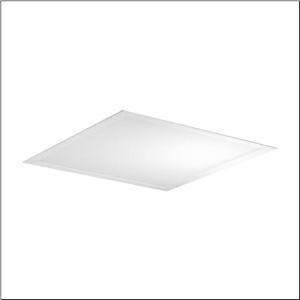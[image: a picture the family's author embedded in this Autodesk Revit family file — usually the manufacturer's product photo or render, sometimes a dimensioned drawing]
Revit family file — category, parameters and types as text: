
# Revit family: apollon_r__31_square_51mp11w72342_58c9
name_source: partatom
category: Lighting Fixtures
units: mm (PartAtom-declared; Revit-internal decimal feet)

## family parameters
Cut with Voids When Loaded = No
Host = Face
Light Source = No
Part Type = Normal
Room Calculation Point = No
Round Connector Dimension = Use Diameter
Shared = No

## types (1)
- Apollon® 31 square (1 x LED, 3800 lm, 27.5 W, 3000K)
    Apparent Load = 28 VA
    CIE Flux Codes = 61 87 97 100 100
    Color Rendering = 80
    Color Temperature = 3000K
    Default Elevation = 1800 mm
    Description = Apollon® 31 square, office luminaire, primary optical cover: micro prismatic cover, of PMMA, CAT 2 (L<= 3000cd/m²), light emission: direct distribution, primary light characteristic: symmetric, installation type: lay-in mounting, LED, rated luminous flux: 3.800lm, luminous efficacy: 138lm/W, light colour: 830, colour temperature: 3000K, with terminal, 3-pole, mains connection: 220..240V, AC, 50/60Hz, rated input power: 28W, housing, of aluminium, traffic white (RAL 9016), module: M625, length: 620mm, width: 620mm, height: 32mm, housing upper side, of sheet steel, galvanised, protection rating (complete): IP20, protection rating (on room side): IP40, insulation class (complete): insulation class II (safety insulation), certification: CE, ENEC, impact resistance: IK03, permissible operating ambient temperature: -20..+40°C, permissible storage temperature: -20..+60°C, packaging unit: 1 piece
    Height = 0 mm  [stored 0 ft]
    Lamp = 1 x LED
    Lamp Light Flux = 3800 lm
    Lamp Power = 27.5 W
    Lamp count = 1
    Length = 620 mm
    Luminous efficacy = 138 lm/W
    Manufacturer = Siteco
    ModVariant = No
    Model = 51MP11W72342
    Mounting Place = Ceiling
    Mounting Type = Recessed
    Number of Poles = 1
    OnlyDefault = Yes
    Power Factor = 1
    Product Name = Apollon® 31 square
    Product group = office luminaire | ceiling recessed
    ProductGroupID = 401
    Protection Class = Protection class II
    Protection Degree = IP 20
    RLX_Detail_Level = 1
    RLX_Emergency_Light_Flux = 0 lm
    RLX_Emergency_Type = 0
    RLX_Emergency_Type_DB = No
    RlxData = <blob elided: 12933 chars, md5=674a0db6>
    Socket = socket
    Standby Power = 0 W
    System Light Flux = 3800 lm
    System Power = 28 W
    Type Comments = Product without accessories
    Type Image = l_1291039.jpg
    URL = http://relux.com
    VarID = ---
    Voltage = 0 V
    Weight = 0.00 kg
    Width = 620 mm

note: [stored X ft] marks values corroborated as IEEE doubles in the binary element streams (Revit-internal decimal feet)

## geometry (parser evidence)
native form markers: Sweep x11
no freeform markers — native parametric forms only
